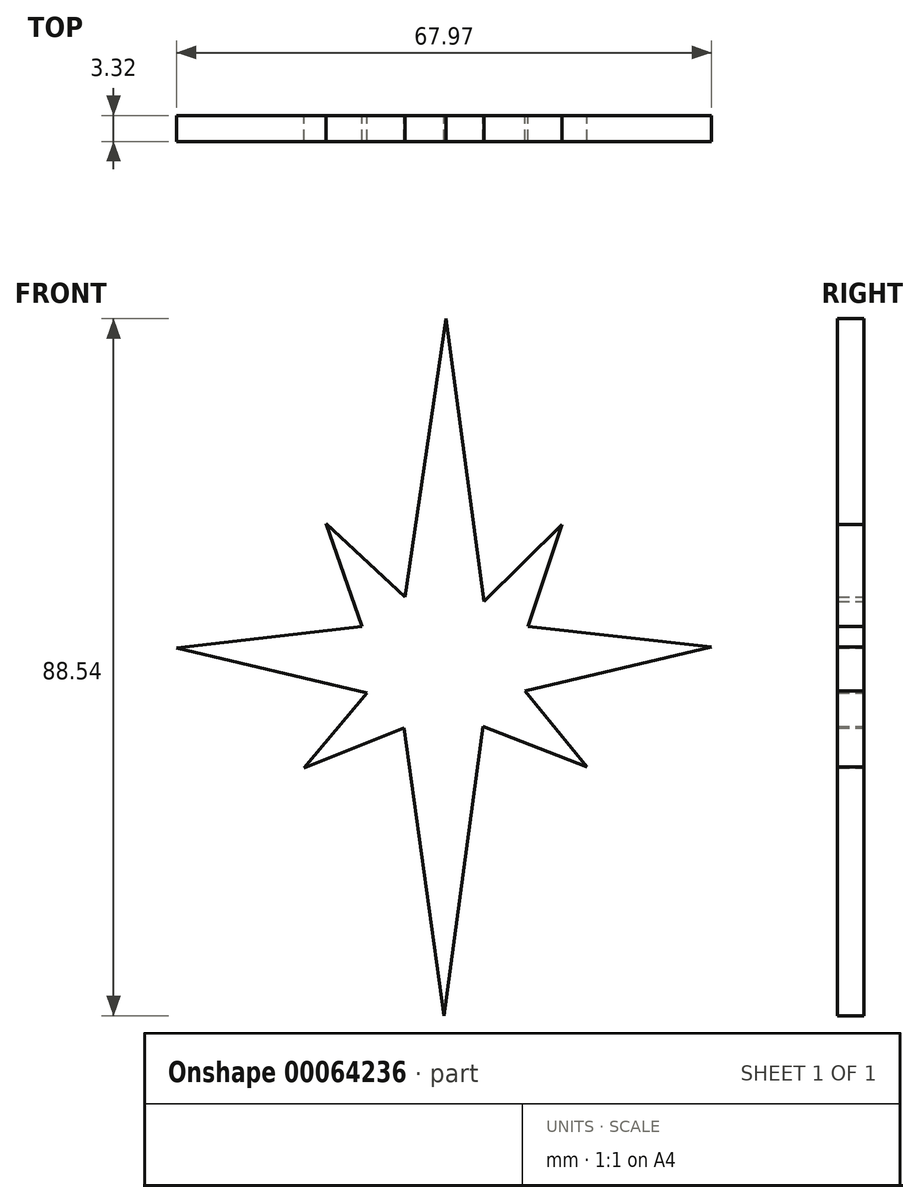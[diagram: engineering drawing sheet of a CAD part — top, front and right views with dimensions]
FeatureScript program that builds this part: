
annotation { "Feature Type Name" : "Feature", "Feature Type Description" : "" }
export const myFeature = defineFeature(function(context is Context, id is Id, definition is map)
    precondition{}
    {
        {
            var Q0;
            Q0=qCreatedBy(makeId("Front.planeOp"),FACE);
            var sketch = newSketch(context, id + "F0", { "sketchPlane" : qUnion([Q0])});
            skLineSegment(sketch, "E0", {"start": v(-16.53, 29.83) * mm, "end": v(0.8, 147.56) * mm});
            skLineSegment(sketch, "E1", {"start": v(0.8, 147.56) * mm, "end": v(16.93, 27.82) * mm});
            skLineSegment(sketch, "E2", {"start": v(16.93, 27.82) * mm, "end": v(50, 60.48) * mm});
            skLineSegment(sketch, "E3", {"start": v(50, 60.48) * mm, "end": v(35.48, 17.34) * mm});
            skLineSegment(sketch, "E4", {"start": v(35.48, 17.34) * mm, "end": v(113.3, 8.47) * mm});
            skLineSegment(sketch, "E5", {"start": v(113.3, 8.47) * mm, "end": v(34.27, -10.08) * mm});
            skLineSegment(sketch, "E6", {"start": v(34.27, -10.08) * mm, "end": v(60.48, -42.33) * mm});
            skLineSegment(sketch, "E7", {"start": v(60.48, -42.33) * mm, "end": v(16.53, -25) * mm});
            skLineSegment(sketch, "E8", {"start": v(16.53, -25) * mm, "end": v(0, -147.56) * mm});
            skLineSegment(sketch, "E9", {"start": v(0, -147.56) * mm, "end": v(-16.93, -25.8) * mm});
            skLineSegment(sketch, "E10", {"start": v(-16.93, -25.8) * mm, "end": v(-59.27, -42.74) * mm});
            skLineSegment(sketch, "E11", {"start": v(-59.27, -42.74) * mm, "end": v(-32.66, -10.89) * mm});
            skLineSegment(sketch, "E12", {"start": v(-32.66, -10.89) * mm, "end": v(-113.3, 8.06) * mm});
            skLineSegment(sketch, "E13", {"start": v(-113.3, 8.06) * mm, "end": v(-34.67, 17.34) * mm});
            skLineSegment(sketch, "E14", {"start": v(-34.67, 17.34) * mm, "end": v(-50, 60.88) * mm});
            skLineSegment(sketch, "E15", {"start": v(-50, 60.88) * mm, "end": v(-16.53, 29.83) * mm});
            skSolve(sketch);
        }
        {
            var Q0;
            Q0=makeQuery(id+"F0.imprint","IMPRINT",FACE,{"disambiguationData":[TD([[makeQuery(id+"F0.imprint","IMPRINT",EDGE,{"derivedFrom":sQuery(id+"F0.wireOp",EDGE,"E0")}),-1.0]])]});
            extrude(context, id + "F1", {"entities" : qUnion([Q0]), "depth" : 11.06 * mm});
        }
        {
            var Q0;
            Q0=makeQuery(id+"F1.opExtrude","SWEPT_BODY",BODY,{"disambiguationData":[OSD([sQuery(id+"F0.wireOp",EDGE,"E0"),sQuery(id+"F0.wireOp",EDGE,"E1"),sQuery(id+"F0.wireOp",EDGE,"E2"),sQuery(id+"F0.wireOp",EDGE,"E3"),sQuery(id+"F0.wireOp",EDGE,"E4"),sQuery(id+"F0.wireOp",EDGE,"E5"),sQuery(id+"F0.wireOp",EDGE,"E6"),sQuery(id+"F0.wireOp",EDGE,"E7"),sQuery(id+"F0.wireOp",EDGE,"E8"),sQuery(id+"F0.wireOp",EDGE,"E9"),sQuery(id+"F0.wireOp",EDGE,"E10"),sQuery(id+"F0.wireOp",EDGE,"E11"),sQuery(id+"F0.wireOp",EDGE,"E12"),sQuery(id+"F0.wireOp",EDGE,"E13"),sQuery(id+"F0.wireOp",EDGE,"E14"),sQuery(id+"F0.wireOp",EDGE,"E15")])]});
            var Q1;
            Q1=makeQuery(id+"F1.opExtrude","CAP_VERTEX",VERTEX,{"disambiguationData":[OSD([sQuery(id+"F0.wireOp",EDGE,"E0"),sQuery(id+"F0.wireOp",EDGE,"E1")])],"isStart":false});
            transform(context, id + "F2", {"entities" : qUnion([Q0]), "transformType" : TransformType.SCALE_UNIFORMLY, "scale" : .3, "scalePoint" : qUnion([Q1]), "makeCopy" : false});
        }
        {
            var Q0;
            Q0=makeQuery(id+"F1.opExtrude","SWEPT_BODY",BODY,{"disambiguationData":[OSD([sQuery(id+"F0.wireOp",EDGE,"E0"),sQuery(id+"F0.wireOp",EDGE,"E1"),sQuery(id+"F0.wireOp",EDGE,"E2"),sQuery(id+"F0.wireOp",EDGE,"E3"),sQuery(id+"F0.wireOp",EDGE,"E4"),sQuery(id+"F0.wireOp",EDGE,"E5"),sQuery(id+"F0.wireOp",EDGE,"E6"),sQuery(id+"F0.wireOp",EDGE,"E7"),sQuery(id+"F0.wireOp",EDGE,"E8"),sQuery(id+"F0.wireOp",EDGE,"E9"),sQuery(id+"F0.wireOp",EDGE,"E10"),sQuery(id+"F0.wireOp",EDGE,"E11"),sQuery(id+"F0.wireOp",EDGE,"E12"),sQuery(id+"F0.wireOp",EDGE,"E13"),sQuery(id+"F0.wireOp",EDGE,"E14"),sQuery(id+"F0.wireOp",EDGE,"E15")])]});
            transform(context, id + "F3", {"entities" : qUnion([Q0]), "transformType" : TransformType.TRANSLATION_3D, "dx" : 59.92 * mm, "dy" : 0 * mm, "dz" : -43.45 * mm, "makeCopy" : false});
        }
    });
